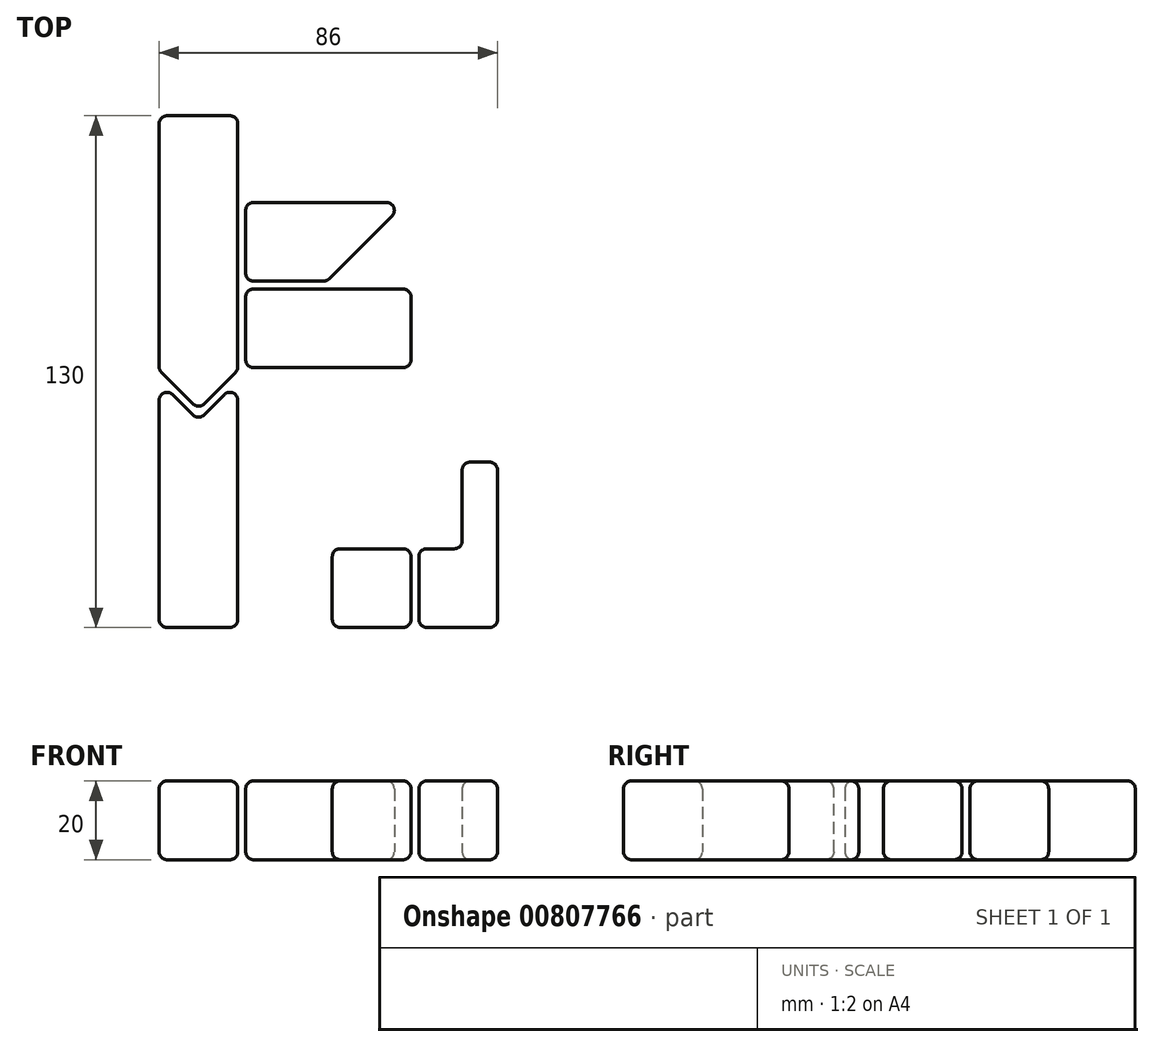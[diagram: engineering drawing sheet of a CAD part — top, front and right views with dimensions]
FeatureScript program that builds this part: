
annotation { "Feature Type Name" : "Feature", "Feature Type Description" : "" }
export const myFeature = defineFeature(function(context is Context, id is Id, definition is map)
    precondition{}
    {
        {
            var Q0;
            Q0=qCreatedBy(makeId("Top.planeOp"),FACE);
            var sketch = newSketch(context, id + "F0", { "sketchPlane" : qUnion([Q0])});
            skPoint(sketch, "E0.middle", {"position": v(0, 0) * mm});
            skLineSegment(sketch, "E1.bottom", {"start": v(0, -22) * mm, "end": v(-22, -22) * mm});
            skLineSegment(sketch, "E1.top", {"start": v(0, 0) * mm, "end": v(-22, 0) * mm});
            skLineSegment(sketch, "E1.left", {"start": v(0, -22) * mm, "end": v(0, 0) * mm});
            skLineSegment(sketch, "E1.right", {"start": v(-22, -22) * mm, "end": v(-22, 0) * mm});
            skLineSegment(sketch, "E2.bottom", {"start": v(0, 0) * mm, "end": v(22, 0) * mm});
            skLineSegment(sketch, "E2.top", {"start": v(0, -22) * mm, "end": v(22, -22) * mm});
            skLineSegment(sketch, "E2.left", {"start": v(0, 0) * mm, "end": v(0, -22) * mm});
            skLineSegment(sketch, "E2.right", {"start": v(22, 0) * mm, "end": v(22, -22) * mm});
            skLineSegment(sketch, "E3.bottom", {"start": v(-22, 0) * mm, "end": v(0, 0) * mm});
            skLineSegment(sketch, "E3.top", {"start": v(-22, 22) * mm, "end": v(0, 22) * mm});
            skLineSegment(sketch, "E3.left", {"start": v(-22, 0) * mm, "end": v(-22, 22) * mm});
            skLineSegment(sketch, "E3.right", {"start": v(0, 0) * mm, "end": v(0, 22) * mm});
            skLineSegment(sketch, "E4.bottom", {"start": v(0, 22) * mm, "end": v(22, 22) * mm});
            skLineSegment(sketch, "E4.left", {"start": v(0, 22) * mm, "end": v(0, 0) * mm});
            skLineSegment(sketch, "E4.right", {"start": v(22, 22) * mm, "end": v(22, 0) * mm});
            skLineSegment(sketch, "E5.bottom", {"start": v(-22, 22) * mm, "end": v(22, 22) * mm});
            skLineSegment(sketch, "E5.top", {"start": v(-22, 44) * mm, "end": v(22, 44) * mm});
            skLineSegment(sketch, "E5.left", {"start": v(-22, 22) * mm, "end": v(-22, 44) * mm});
            skLineSegment(sketch, "E5.right", {"start": v(22, 22) * mm, "end": v(22, 44) * mm});
            skLineSegment(sketch, "E6.bottom", {"start": v(22, 44) * mm, "end": v(-22, 44) * mm});
            skLineSegment(sketch, "E6.top", {"start": v(22, 66) * mm, "end": v(-22, 66) * mm});
            skLineSegment(sketch, "E6.left", {"start": v(22, 44) * mm, "end": v(22, 66) * mm});
            skLineSegment(sketch, "E6.right", {"start": v(-22, 44) * mm, "end": v(-22, 66) * mm});
            skLineSegment(sketch, "E7.bottom", {"start": v(22, -22) * mm, "end": v(44, -22) * mm});
            skLineSegment(sketch, "E7.top", {"start": v(22, 44) * mm, "end": v(44, 44) * mm});
            skLineSegment(sketch, "E7.left", {"start": v(22, -22) * mm, "end": v(22, 44) * mm});
            skLineSegment(sketch, "E7.right", {"start": v(44, -22) * mm, "end": v(44, 44) * mm});
            skLineSegment(sketch, "E8.top", {"start": v(22, 66) * mm, "end": v(44, 66) * mm});
            skLineSegment(sketch, "E8.right", {"start": v(44, 44) * mm, "end": v(44, 66) * mm});
            skLineSegment(sketch, "E9.bottom", {"start": v(-22, -22) * mm, "end": v(-44, -22) * mm});
            skLineSegment(sketch, "E9.top", {"start": v(-22, 44) * mm, "end": v(-44, 44) * mm, "construction": true});
            skLineSegment(sketch, "E9.left", {"start": v(-22, -22) * mm, "end": v(-22, 44) * mm});
            skLineSegment(sketch, "E9.right", {"start": v(-44, -22) * mm, "end": v(-44, 44) * mm});
            skLineSegment(sketch, "E10.bottom", {"start": v(22, 0) * mm, "end": v(44, 0) * mm, "construction": true});
            skLineSegment(sketch, "E10.top", {"start": v(22, 22) * mm, "end": v(44, 22) * mm, "construction": true});
            skLineSegment(sketch, "E10.left", {"start": v(22, 0) * mm, "end": v(22, 22) * mm, "construction": true});
            skLineSegment(sketch, "E10.right", {"start": v(44, 0) * mm, "end": v(44, 22) * mm, "construction": true});
            skLineSegment(sketch, "E11", {"start": v(33, 22) * mm, "end": v(33, 0) * mm});
            skLineSegment(sketch, "E12", {"start": v(33, 22) * mm, "end": v(44, 22) * mm});
            skLineSegment(sketch, "E13", {"start": v(33, 0) * mm, "end": v(22, 0) * mm});
            skLineSegment(sketch, "E14.bottom", {"start": v(-22, 66) * mm, "end": v(44, 66) * mm});
            skLineSegment(sketch, "E14.top", {"start": v(-22, 88) * mm, "end": v(44, 88) * mm});
            skLineSegment(sketch, "E14.left", {"start": v(-22, 66) * mm, "end": v(-22, 88) * mm});
            skLineSegment(sketch, "E14.right", {"start": v(44, 66) * mm, "end": v(44, 88) * mm});
            skLineSegment(sketch, "E15", {"start": v(0, 88) * mm, "end": v(0, 66) * mm, "construction": true});
            skLineSegment(sketch, "E16", {"start": v(22, 66) * mm, "end": v(22, 88) * mm, "construction": true});
            skLineSegment(sketch, "E17", {"start": v(22, 88) * mm, "end": v(0, 66) * mm});
            skLineSegment(sketch, "E18.bottom", {"start": v(-22, 88) * mm, "end": v(0, 88) * mm});
            skLineSegment(sketch, "E18.top", {"start": v(-22, 110) * mm, "end": v(0, 110) * mm});
            skLineSegment(sketch, "E18.left", {"start": v(-22, 88) * mm, "end": v(-22, 110) * mm});
            skLineSegment(sketch, "E18.right", {"start": v(0, 88) * mm, "end": v(0, 110) * mm});
            skLineSegment(sketch, "E19.bottom", {"start": v(0, 110) * mm, "end": v(22, 110) * mm});
            skLineSegment(sketch, "E19.top", {"start": v(0, 88) * mm, "end": v(22, 88) * mm});
            skLineSegment(sketch, "E19.left", {"start": v(0, 110) * mm, "end": v(0, 88) * mm});
            skLineSegment(sketch, "E19.right", {"start": v(22, 110) * mm, "end": v(22, 88) * mm});
            skLineSegment(sketch, "E20.bottom", {"start": v(22, 110) * mm, "end": v(44, 110) * mm});
            skLineSegment(sketch, "E20.top", {"start": v(22, 88) * mm, "end": v(44, 88) * mm});
            skLineSegment(sketch, "E20.right", {"start": v(44, 110) * mm, "end": v(44, 88) * mm});
            skLineSegment(sketch, "E21", {"start": v(-22, 110) * mm, "end": v(-44, 110) * mm});
            skLineSegment(sketch, "E22", {"start": v(-44, 110) * mm, "end": v(-44, 44) * mm});
            skLineSegment(sketch, "E23", {"start": v(-44, 44) * mm, "end": v(-22, 22) * mm, "construction": true});
            skLineSegment(sketch, "E24", {"start": v(-22, 44) * mm, "end": v(-44, 22) * mm, "construction": true});
            skLineSegment(sketch, "E25", {"start": v(-44, 44) * mm, "end": v(-33, 33) * mm});
            skLineSegment(sketch, "E26", {"start": v(-33, 33) * mm, "end": v(-22, 44) * mm});
            skSolve(sketch);
        }
        {
            var Q0;
            Q0=qCreatedBy(makeId("Top.planeOp"),FACE);
            var sketch = newSketch(context, id + "F1", { "sketchPlane" : qUnion([Q0])});
            skLineSegment(sketch, "E27.0", {"start": v(-23, 9) * mm, "end": v(-23, 44.41) * mm});
            skLineSegment(sketch, "E27.1", {"start": v(-33, 34.41) * mm, "end": v(-23, 44.41) * mm});
            skLineSegment(sketch, "E27.2", {"start": v(-23, 12) * mm, "end": v(-23, 109) * mm});
            skLineSegment(sketch, "E27.3", {"start": v(-23, 109) * mm, "end": v(-43, 109) * mm});
            skLineSegment(sketch, "E27.4", {"start": v(-43, 109) * mm, "end": v(-43, 44.41) * mm});
            skLineSegment(sketch, "E27.5", {"start": v(-23, 9) * mm, "end": v(-23, 12) * mm});
            skLineSegment(sketch, "E27.6", {"start": v(-43, 44.41) * mm, "end": v(-33, 34.41) * mm});
            skLineSegment(sketch, "E28.0", {"start": v(-1, 89) * mm, "end": v(-1, 109) * mm});
            skLineSegment(sketch, "E28.1", {"start": v(-21, 89) * mm, "end": v(-1, 89) * mm});
            skLineSegment(sketch, "E28.2", {"start": v(-21, 109) * mm, "end": v(-21, 89) * mm});
            skLineSegment(sketch, "E28.3", {"start": v(-1, 109) * mm, "end": v(-21, 109) * mm});
            skLineSegment(sketch, "E29.0", {"start": v(21, 109) * mm, "end": v(1, 109) * mm});
            skLineSegment(sketch, "E29.1", {"start": v(21, 89) * mm, "end": v(21, 109) * mm});
            skLineSegment(sketch, "E29.2", {"start": v(1, 89) * mm, "end": v(21, 89) * mm});
            skLineSegment(sketch, "E29.3", {"start": v(1, 109) * mm, "end": v(1, 89) * mm});
            skLineSegment(sketch, "E30.0", {"start": v(43, 109) * mm, "end": v(23, 109) * mm});
            skLineSegment(sketch, "E30.1", {"start": v(43, 89) * mm, "end": v(43, 109) * mm});
            skLineSegment(sketch, "E30.2", {"start": v(23, 89) * mm, "end": v(43, 89) * mm});
            skLineSegment(sketch, "E30.3", {"start": v(23, 109) * mm, "end": v(23, 89) * mm});
            skLineSegment(sketch, "E31.0", {"start": v(19.59, 87) * mm, "end": v(0, 87) * mm});
            skLineSegment(sketch, "E31.1", {"start": v(-0.41, 67) * mm, "end": v(19.59, 87) * mm});
            skLineSegment(sketch, "E31.2", {"start": v(0, 87) * mm, "end": v(-21, 87) * mm});
            skLineSegment(sketch, "E31.3", {"start": v(-21, 87) * mm, "end": v(-21, 67) * mm});
            skLineSegment(sketch, "E31.4", {"start": v(-21, 67) * mm, "end": v(-0.41, 67) * mm});
            skLineSegment(sketch, "E32.0", {"start": v(22.41, 87) * mm, "end": v(2.41, 67) * mm});
            skLineSegment(sketch, "E32.1", {"start": v(43, 87) * mm, "end": v(22.41, 87) * mm});
            skLineSegment(sketch, "E32.2", {"start": v(2.41, 67) * mm, "end": v(27, 67) * mm});
            skLineSegment(sketch, "E32.3", {"start": v(27, 67) * mm, "end": v(43, 67) * mm});
            skLineSegment(sketch, "E32.4", {"start": v(43, 67) * mm, "end": v(43, 87) * mm});
            skLineSegment(sketch, "E33.0", {"start": v(21, 45) * mm, "end": v(21, 65) * mm});
            skLineSegment(sketch, "E33.1", {"start": v(-21, 45) * mm, "end": v(21, 45) * mm});
            skLineSegment(sketch, "E33.2", {"start": v(21, 65) * mm, "end": v(0, 65) * mm});
            skLineSegment(sketch, "E33.3", {"start": v(0, 65) * mm, "end": v(-21, 65) * mm});
            skLineSegment(sketch, "E33.4", {"start": v(-21, 65) * mm, "end": v(-21, 45) * mm});
            skLineSegment(sketch, "E34.0", {"start": v(23, 65) * mm, "end": v(23, 45) * mm});
            skLineSegment(sketch, "E34.1", {"start": v(43, 65) * mm, "end": v(23, 65) * mm});
            skLineSegment(sketch, "E34.2", {"start": v(43, 45) * mm, "end": v(43, 65) * mm});
            skLineSegment(sketch, "E34.3", {"start": v(23, 45) * mm, "end": v(43, 45) * mm});
            skLineSegment(sketch, "E35.0", {"start": v(-21, 23) * mm, "end": v(0, 23) * mm});
            skLineSegment(sketch, "E35.1", {"start": v(-21, 43) * mm, "end": v(-21, 23) * mm});
            skLineSegment(sketch, "E35.2", {"start": v(0, 23) * mm, "end": v(21, 23) * mm});
            skLineSegment(sketch, "E35.3", {"start": v(21, 23) * mm, "end": v(21, 43) * mm});
            skLineSegment(sketch, "E35.4", {"start": v(21, 43) * mm, "end": v(-21, 43) * mm});
            skLineSegment(sketch, "E36.0", {"start": v(32, 1) * mm, "end": v(32, 23) * mm});
            skLineSegment(sketch, "E36.1", {"start": v(23, 1) * mm, "end": v(32, 1) * mm});
            skLineSegment(sketch, "E36.2", {"start": v(43, 23) * mm, "end": v(43, 43) * mm});
            skLineSegment(sketch, "E36.3", {"start": v(43, 43) * mm, "end": v(23, 43) * mm});
            skLineSegment(sketch, "E36.4", {"start": v(23, 43) * mm, "end": v(23, 27) * mm});
            skLineSegment(sketch, "E36.5", {"start": v(32, 23) * mm, "end": v(43, 23) * mm});
            skLineSegment(sketch, "E36.6", {"start": v(23, 27) * mm, "end": v(23, 1) * mm});
            skLineSegment(sketch, "E37.0", {"start": v(34, -1) * mm, "end": v(23, -1) * mm});
            skLineSegment(sketch, "E37.1", {"start": v(23, -21) * mm, "end": v(43, -21) * mm});
            skLineSegment(sketch, "E37.2", {"start": v(43, -21) * mm, "end": v(43, 21) * mm});
            skLineSegment(sketch, "E37.3", {"start": v(23, -1) * mm, "end": v(23, -21) * mm});
            skLineSegment(sketch, "E37.4", {"start": v(43, 21) * mm, "end": v(34, 21) * mm});
            skLineSegment(sketch, "E37.5", {"start": v(34, 21) * mm, "end": v(34, -1) * mm});
            skLineSegment(sketch, "E38.0", {"start": v(-43, 41.59) * mm, "end": v(-43, -21) * mm});
            skLineSegment(sketch, "E38.1", {"start": v(-33, 31.59) * mm, "end": v(-43, 41.59) * mm});
            skLineSegment(sketch, "E38.2", {"start": v(-23, -21) * mm, "end": v(-23, 0) * mm});
            skLineSegment(sketch, "E38.3", {"start": v(-23, 0) * mm, "end": v(-23, 27) * mm});
            skLineSegment(sketch, "E38.4", {"start": v(-23, 27) * mm, "end": v(-23, 41.59) * mm});
            skLineSegment(sketch, "E38.5", {"start": v(-43, -21) * mm, "end": v(-23, -21) * mm});
            skLineSegment(sketch, "E38.6", {"start": v(-23, 41.59) * mm, "end": v(-33, 31.59) * mm});
            skLineSegment(sketch, "E39.0", {"start": v(-1, 21) * mm, "end": v(-21, 21) * mm});
            skLineSegment(sketch, "E39.1", {"start": v(-1, 1) * mm, "end": v(-1, 21) * mm});
            skLineSegment(sketch, "E39.2", {"start": v(-21, 1) * mm, "end": v(-1, 1) * mm});
            skLineSegment(sketch, "E39.3", {"start": v(-21, 21) * mm, "end": v(-21, 1) * mm});
            skLineSegment(sketch, "E40.0", {"start": v(1, 1) * mm, "end": v(21, 1) * mm});
            skLineSegment(sketch, "E40.1", {"start": v(1, 21) * mm, "end": v(1, 1) * mm});
            skLineSegment(sketch, "E40.2", {"start": v(21, 21) * mm, "end": v(1, 21) * mm});
            skLineSegment(sketch, "E40.3", {"start": v(21, 1) * mm, "end": v(21, 21) * mm});
            skLineSegment(sketch, "E41.0", {"start": v(-21, -1) * mm, "end": v(-21, -21) * mm});
            skLineSegment(sketch, "E41.1", {"start": v(-1, -1) * mm, "end": v(-21, -1) * mm});
            skLineSegment(sketch, "E41.2", {"start": v(-1, -21) * mm, "end": v(-1, -1) * mm});
            skLineSegment(sketch, "E41.3", {"start": v(-21, -21) * mm, "end": v(-1, -21) * mm});
            skLineSegment(sketch, "E42.0", {"start": v(1, -21) * mm, "end": v(21, -21) * mm});
            skLineSegment(sketch, "E42.1", {"start": v(1, -1) * mm, "end": v(1, -21) * mm});
            skLineSegment(sketch, "E42.2", {"start": v(21, -1) * mm, "end": v(1, -1) * mm});
            skLineSegment(sketch, "E42.3", {"start": v(21, -21) * mm, "end": v(21, -1) * mm});
            skSolve(sketch);
        }
        {
            var Q0;
            Q0 = qSketchRegion(id + "F1", true);
            extrude(context, id + "F2", {"entities" : qUnion([Q0]), "endBound" : BoundingType.SYMMETRIC, "depth" : 20 * mm, "offsetDistance" : 25 * mm});
        }
        {
            var Q0;
            Q0=makeQuery(id+"F2.opExtrude","SWEPT_BODY",BODY,{"disambiguationData":[OSD([sQuery(id+"F1.wireOp",EDGE,"E41.0"),sQuery(id+"F1.wireOp",EDGE,"E41.1"),sQuery(id+"F1.wireOp",EDGE,"E41.2"),sQuery(id+"F1.wireOp",EDGE,"E41.3")])]});
            var Q1;
            Q1=makeQuery(id+"F2.opExtrude","SWEPT_BODY",BODY,{"disambiguationData":[OSD([sQuery(id+"F1.wireOp",EDGE,"E39.0"),sQuery(id+"F1.wireOp",EDGE,"E39.1"),sQuery(id+"F1.wireOp",EDGE,"E39.2"),sQuery(id+"F1.wireOp",EDGE,"E39.3")])]});
            var Q2;
            Q2=makeQuery(id+"F2.opExtrude","SWEPT_BODY",BODY,{"disambiguationData":[OSD([sQuery(id+"F1.wireOp",EDGE,"E40.0"),sQuery(id+"F1.wireOp",EDGE,"E40.1"),sQuery(id+"F1.wireOp",EDGE,"E40.2"),sQuery(id+"F1.wireOp",EDGE,"E40.3")])]});
            var Q3;
            Q3=makeQuery(id+"F2.opExtrude","SWEPT_BODY",BODY,{"disambiguationData":[OSD([sQuery(id+"F1.wireOp",EDGE,"E36.0"),sQuery(id+"F1.wireOp",EDGE,"E36.1"),sQuery(id+"F1.wireOp",EDGE,"E36.2"),sQuery(id+"F1.wireOp",EDGE,"E36.3"),sQuery(id+"F1.wireOp",EDGE,"E36.4"),sQuery(id+"F1.wireOp",EDGE,"E36.5"),sQuery(id+"F1.wireOp",EDGE,"E36.6")])]});
            var Q4;
            Q4=makeQuery(id+"F2.opExtrude","SWEPT_BODY",BODY,{"disambiguationData":[OSD([sQuery(id+"F1.wireOp",EDGE,"E34.0"),sQuery(id+"F1.wireOp",EDGE,"E34.1"),sQuery(id+"F1.wireOp",EDGE,"E34.2"),sQuery(id+"F1.wireOp",EDGE,"E34.3")])]});
            var Q5;
            Q5=makeQuery(id+"F2.opExtrude","SWEPT_BODY",BODY,{"disambiguationData":[OSD([sQuery(id+"F1.wireOp",EDGE,"E35.0"),sQuery(id+"F1.wireOp",EDGE,"E35.1"),sQuery(id+"F1.wireOp",EDGE,"E35.2"),sQuery(id+"F1.wireOp",EDGE,"E35.3"),sQuery(id+"F1.wireOp",EDGE,"E35.4")])]});
            var Q6;
            Q6=makeQuery(id+"F2.opExtrude","SWEPT_BODY",BODY,{"disambiguationData":[OSD([sQuery(id+"F1.wireOp",EDGE,"E32.0"),sQuery(id+"F1.wireOp",EDGE,"E32.1"),sQuery(id+"F1.wireOp",EDGE,"E32.2"),sQuery(id+"F1.wireOp",EDGE,"E32.3"),sQuery(id+"F1.wireOp",EDGE,"E32.4")])]});
            var Q7;
            Q7=makeQuery(id+"F2.opExtrude","SWEPT_BODY",BODY,{"disambiguationData":[OSD([sQuery(id+"F1.wireOp",EDGE,"E30.0"),sQuery(id+"F1.wireOp",EDGE,"E30.1"),sQuery(id+"F1.wireOp",EDGE,"E30.2"),sQuery(id+"F1.wireOp",EDGE,"E30.3")])]});
            var Q8;
            Q8=makeQuery(id+"F2.opExtrude","SWEPT_BODY",BODY,{"disambiguationData":[OSD([sQuery(id+"F1.wireOp",EDGE,"E29.0"),sQuery(id+"F1.wireOp",EDGE,"E29.1"),sQuery(id+"F1.wireOp",EDGE,"E29.2"),sQuery(id+"F1.wireOp",EDGE,"E29.3")])]});
            var Q9;
            Q9=makeQuery(id+"F2.opExtrude","SWEPT_BODY",BODY,{"disambiguationData":[OSD([sQuery(id+"F1.wireOp",EDGE,"E28.0"),sQuery(id+"F1.wireOp",EDGE,"E28.1"),sQuery(id+"F1.wireOp",EDGE,"E28.2"),sQuery(id+"F1.wireOp",EDGE,"E28.3")])]});
            deleteBodies(context, id + "F3", {"entities" : qUnion([Q0, Q1, Q2, Q3, Q4, Q5, Q6, Q7, Q8, Q9])});
        }
        {
            var Q0;
            Q0=makeQuery(id+"F2.opExtrude","CAP_FACE",FACE,{"disambiguationData":[OSD([sQuery(id+"F1.wireOp",EDGE,"E42.0"),sQuery(id+"F1.wireOp",EDGE,"E42.1"),sQuery(id+"F1.wireOp",EDGE,"E42.2"),sQuery(id+"F1.wireOp",EDGE,"E42.3")])],"isStart":false});
            var Q1;
            Q1=makeQuery(id+"F2.opExtrude","CAP_FACE",FACE,{"disambiguationData":[OSD([sQuery(id+"F1.wireOp",EDGE,"E42.0"),sQuery(id+"F1.wireOp",EDGE,"E42.1"),sQuery(id+"F1.wireOp",EDGE,"E42.2"),sQuery(id+"F1.wireOp",EDGE,"E42.3")])],"isStart":true});
            var Q2;
            Q2=makeQuery(id+"F2.opExtrude","SWEPT_FACE",FACE,{"disambiguationData":[OSD([sQuery(id+"F1.wireOp",EDGE,"E42.0")])]});
            var Q3;
            Q3=makeQuery(id+"F2.opExtrude","SWEPT_FACE",FACE,{"disambiguationData":[OSD([sQuery(id+"F1.wireOp",EDGE,"E42.1")])]});
            var Q4;
            Q4=makeQuery(id+"F2.opExtrude","SWEPT_FACE",FACE,{"disambiguationData":[OSD([sQuery(id+"F1.wireOp",EDGE,"E42.3")])]});
            var Q5;
            Q5=makeQuery(id+"F2.opExtrude","SWEPT_FACE",FACE,{"disambiguationData":[OSD([sQuery(id+"F1.wireOp",EDGE,"E42.2")])]});
            fillet(context, id + "F4", {"entities" : qUnion([Q0, Q1, Q2, Q3, Q4, Q5]), "radius" : 2 * mm, "tangentPropagation" : true, "allowEdgeOverflow" : false});
        }
        {
            var Q0;
            Q0=makeQuery(id+"F2.opExtrude","SWEPT_FACE",FACE,{"disambiguationData":[OSD([sQuery(id+"F1.wireOp",EDGE,"E33.0")])]});
            var Q1;
            Q1=makeQuery(id+"F2.opExtrude","SWEPT_FACE",FACE,{"disambiguationData":[OSD([sQuery(id+"F1.wireOp",EDGE,"E33.1")])]});
            var Q2;
            Q2=makeQuery(id+"F2.opExtrude","CAP_FACE",FACE,{"disambiguationData":[OSD([sQuery(id+"F1.wireOp",EDGE,"E33.0"),sQuery(id+"F1.wireOp",EDGE,"E33.1"),sQuery(id+"F1.wireOp",EDGE,"E33.2"),sQuery(id+"F1.wireOp",EDGE,"E33.3"),sQuery(id+"F1.wireOp",EDGE,"E33.4")])],"isStart":false});
            var Q3;
            Q3=makeQuery(id+"F2.opExtrude","CAP_FACE",FACE,{"disambiguationData":[OSD([sQuery(id+"F1.wireOp",EDGE,"E33.0"),sQuery(id+"F1.wireOp",EDGE,"E33.1"),sQuery(id+"F1.wireOp",EDGE,"E33.2"),sQuery(id+"F1.wireOp",EDGE,"E33.3"),sQuery(id+"F1.wireOp",EDGE,"E33.4")])],"isStart":true});
            var Q4;
            Q4=makeQuery(id+"F2.opExtrude","SWEPT_FACE",FACE,{"disambiguationData":[OSD([sQuery(id+"F1.wireOp",EDGE,"E33.2"),sQuery(id+"F1.wireOp",EDGE,"E33.3")])]});
            var Q5;
            Q5=makeQuery(id+"F2.opExtrude","SWEPT_FACE",FACE,{"disambiguationData":[OSD([sQuery(id+"F1.wireOp",EDGE,"E33.4")])]});
            fillet(context, id + "F5", {"entities" : qUnion([Q0, Q1, Q2, Q3, Q4, Q5]), "radius" : 2 * mm, "tangentPropagation" : true, "allowEdgeOverflow" : false});
        }
        {
            var Q0;
            Q0=makeQuery(id+"F2.opExtrude","CAP_FACE",FACE,{"disambiguationData":[OSD([sQuery(id+"F1.wireOp",EDGE,"E37.0"),sQuery(id+"F1.wireOp",EDGE,"E37.1"),sQuery(id+"F1.wireOp",EDGE,"E37.2"),sQuery(id+"F1.wireOp",EDGE,"E37.3"),sQuery(id+"F1.wireOp",EDGE,"E37.4"),sQuery(id+"F1.wireOp",EDGE,"E37.5")])],"isStart":true});
            var Q1;
            Q1=makeQuery(id+"F2.opExtrude","CAP_FACE",FACE,{"disambiguationData":[OSD([sQuery(id+"F1.wireOp",EDGE,"E37.0"),sQuery(id+"F1.wireOp",EDGE,"E37.1"),sQuery(id+"F1.wireOp",EDGE,"E37.2"),sQuery(id+"F1.wireOp",EDGE,"E37.3"),sQuery(id+"F1.wireOp",EDGE,"E37.4"),sQuery(id+"F1.wireOp",EDGE,"E37.5")])],"isStart":false});
            var Q2;
            Q2=makeQuery(id+"F2.opExtrude","SWEPT_FACE",FACE,{"disambiguationData":[OSD([sQuery(id+"F1.wireOp",EDGE,"E37.4")])]});
            var Q3;
            Q3=makeQuery(id+"F2.opExtrude","SWEPT_FACE",FACE,{"disambiguationData":[OSD([sQuery(id+"F1.wireOp",EDGE,"E37.0")])]});
            var Q4;
            Q4=makeQuery(id+"F2.opExtrude","SWEPT_FACE",FACE,{"disambiguationData":[OSD([sQuery(id+"F1.wireOp",EDGE,"E37.3")])]});
            var Q5;
            Q5=makeQuery(id+"F2.opExtrude","SWEPT_FACE",FACE,{"disambiguationData":[OSD([sQuery(id+"F1.wireOp",EDGE,"E37.2")])]});
            var Q6;
            Q6=makeQuery(id+"F2.opExtrude","SWEPT_FACE",FACE,{"disambiguationData":[OSD([sQuery(id+"F1.wireOp",EDGE,"E37.1")])]});
            fillet(context, id + "F6", {"entities" : qUnion([Q0, Q1, Q2, Q3, Q4, Q5, Q6]), "radius" : 2 * mm, "tangentPropagation" : true, "allowEdgeOverflow" : false});
        }
        {
            var Q0;
            Q0=makeQuery(id+"F2.opExtrude","CAP_FACE",FACE,{"disambiguationData":[OSD([sQuery(id+"F1.wireOp",EDGE,"E31.0"),sQuery(id+"F1.wireOp",EDGE,"E31.1"),sQuery(id+"F1.wireOp",EDGE,"E31.2"),sQuery(id+"F1.wireOp",EDGE,"E31.3"),sQuery(id+"F1.wireOp",EDGE,"E31.4")])],"isStart":false});
            var Q1;
            Q1=makeQuery(id+"F2.opExtrude","SWEPT_FACE",FACE,{"disambiguationData":[OSD([sQuery(id+"F1.wireOp",EDGE,"E31.3")])]});
            var Q2;
            Q2=makeQuery(id+"F2.opExtrude","CAP_FACE",FACE,{"disambiguationData":[OSD([sQuery(id+"F1.wireOp",EDGE,"E31.0"),sQuery(id+"F1.wireOp",EDGE,"E31.1"),sQuery(id+"F1.wireOp",EDGE,"E31.2"),sQuery(id+"F1.wireOp",EDGE,"E31.3"),sQuery(id+"F1.wireOp",EDGE,"E31.4")])],"isStart":true});
            var Q3;
            Q3=makeQuery(id+"F2.opExtrude","SWEPT_FACE",FACE,{"disambiguationData":[OSD([sQuery(id+"F1.wireOp",EDGE,"E31.1")])]});
            var Q4;
            Q4=makeQuery(id+"F2.opExtrude","SWEPT_FACE",FACE,{"disambiguationData":[OSD([sQuery(id+"F1.wireOp",EDGE,"E31.4")])]});
            var Q5;
            Q5=makeQuery(id+"F2.opExtrude","SWEPT_FACE",FACE,{"disambiguationData":[OSD([sQuery(id+"F1.wireOp",EDGE,"E31.0"),sQuery(id+"F1.wireOp",EDGE,"E31.2")])]});
            fillet(context, id + "F7", {"entities" : qUnion([Q0, Q1, Q2, Q3, Q4, Q5]), "radius" : 2 * mm, "tangentPropagation" : true, "allowEdgeOverflow" : false});
        }
        {
            var Q0;
            Q0=makeQuery(id+"F2.opExtrude","CAP_FACE",FACE,{"disambiguationData":[OSD([sQuery(id+"F1.wireOp",EDGE,"E27.1"),sQuery(id+"F1.wireOp",EDGE,"E27.2"),sQuery(id+"F1.wireOp",EDGE,"E27.3"),sQuery(id+"F1.wireOp",EDGE,"E27.4"),sQuery(id+"F1.wireOp",EDGE,"E27.6")])],"isStart":true});
            var Q1;
            Q1=makeQuery(id+"F2.opExtrude","SWEPT_FACE",FACE,{"disambiguationData":[OSD([sQuery(id+"F1.wireOp",EDGE,"E27.2")])]});
            var Q2;
            Q2=makeQuery(id+"F2.opExtrude","CAP_FACE",FACE,{"disambiguationData":[OSD([sQuery(id+"F1.wireOp",EDGE,"E27.1"),sQuery(id+"F1.wireOp",EDGE,"E27.2"),sQuery(id+"F1.wireOp",EDGE,"E27.3"),sQuery(id+"F1.wireOp",EDGE,"E27.4"),sQuery(id+"F1.wireOp",EDGE,"E27.6")])],"isStart":false});
            var Q3;
            Q3=makeQuery(id+"F2.opExtrude","SWEPT_FACE",FACE,{"disambiguationData":[OSD([sQuery(id+"F1.wireOp",EDGE,"E27.4")])]});
            var Q4;
            Q4=makeQuery(id+"F2.opExtrude","SWEPT_FACE",FACE,{"disambiguationData":[OSD([sQuery(id+"F1.wireOp",EDGE,"E27.6")])]});
            var Q5;
            Q5=makeQuery(id+"F2.opExtrude","SWEPT_FACE",FACE,{"disambiguationData":[OSD([sQuery(id+"F1.wireOp",EDGE,"E27.1")])]});
            var Q6;
            Q6=makeQuery(id+"F2.opExtrude","SWEPT_FACE",FACE,{"disambiguationData":[OSD([sQuery(id+"F1.wireOp",EDGE,"E27.3")])]});
            fillet(context, id + "F8", {"entities" : qUnion([Q0, Q1, Q2, Q3, Q4, Q5, Q6]), "radius" : 2 * mm, "tangentPropagation" : true, "allowEdgeOverflow" : false});
        }
        {
            var Q0;
            Q0=makeQuery(id+"F2.opExtrude","CAP_FACE",FACE,{"disambiguationData":[OSD([sQuery(id+"F1.wireOp",EDGE,"E38.0"),sQuery(id+"F1.wireOp",EDGE,"E38.1"),sQuery(id+"F1.wireOp",EDGE,"E38.2"),sQuery(id+"F1.wireOp",EDGE,"E38.3"),sQuery(id+"F1.wireOp",EDGE,"E38.4"),sQuery(id+"F1.wireOp",EDGE,"E38.5"),sQuery(id+"F1.wireOp",EDGE,"E38.6")])],"isStart":false});
            var Q1;
            Q1=makeQuery(id+"F2.opExtrude","SWEPT_FACE",FACE,{"disambiguationData":[OSD([sQuery(id+"F1.wireOp",EDGE,"E38.2"),sQuery(id+"F1.wireOp",EDGE,"E38.3"),sQuery(id+"F1.wireOp",EDGE,"E38.4")])]});
            var Q2;
            Q2=makeQuery(id+"F2.opExtrude","CAP_FACE",FACE,{"disambiguationData":[OSD([sQuery(id+"F1.wireOp",EDGE,"E38.0"),sQuery(id+"F1.wireOp",EDGE,"E38.1"),sQuery(id+"F1.wireOp",EDGE,"E38.2"),sQuery(id+"F1.wireOp",EDGE,"E38.3"),sQuery(id+"F1.wireOp",EDGE,"E38.4"),sQuery(id+"F1.wireOp",EDGE,"E38.5"),sQuery(id+"F1.wireOp",EDGE,"E38.6")])],"isStart":true});
            var Q3;
            Q3=makeQuery(id+"F2.opExtrude","SWEPT_FACE",FACE,{"disambiguationData":[OSD([sQuery(id+"F1.wireOp",EDGE,"E38.0")])]});
            var Q4;
            Q4=makeQuery(id+"F2.opExtrude","SWEPT_FACE",FACE,{"disambiguationData":[OSD([sQuery(id+"F1.wireOp",EDGE,"E38.5")])]});
            var Q5;
            Q5=makeQuery(id+"F2.opExtrude","SWEPT_FACE",FACE,{"disambiguationData":[OSD([sQuery(id+"F1.wireOp",EDGE,"E38.1")])]});
            var Q6;
            Q6=makeQuery(id+"F2.opExtrude","SWEPT_FACE",FACE,{"disambiguationData":[OSD([sQuery(id+"F1.wireOp",EDGE,"E38.6")])]});
            fillet(context, id + "F9", {"entities" : qUnion([Q0, Q1, Q2, Q3, Q4, Q5, Q6]), "radius" : 2 * mm, "tangentPropagation" : true, "allowEdgeOverflow" : false});
        }
    });
